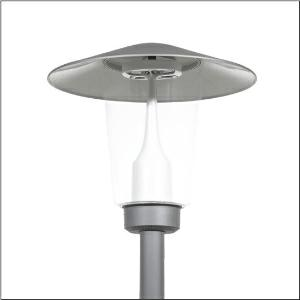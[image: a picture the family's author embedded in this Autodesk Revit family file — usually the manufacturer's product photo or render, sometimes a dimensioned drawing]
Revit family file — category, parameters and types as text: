
# Revit family: pilzleuchte_iq___p1_0a_5xa5235lf14hp_c758
name_source: partatom
category: Lighting Fixtures
units: mm (PartAtom-declared; Revit-internal decimal feet)

## family parameters
Cut with Voids When Loaded = No
Host = Face
Light Source = No
Part Type = Normal
Room Calculation Point = No
Round Connector Dimension = Use Diameter
Shared = No

## types (1)
- --- (1 x LED, 4960 lm, 33.6 W, 4000K)
    Apparent Load = 34 VA
    CIE Flux Codes = 35 64 90 96 100
    Color Rendering = 70
    Color Temperature = 4000K
    Default Elevation = 1800 mm
    Description = Mushroom Luminaire iQ, mast luminaire, Module 540 iQ-SR, primary light control with 3 zone facetted reflector, of plastic, silver coated, highly specular, structured, primary optical cover: cover, of PMMA, transparent, light distribution: P1.0a, light emission: direct distribution, primary light characteristic: strongly asymmetric, installation type: post-top, LED, High Power LED, rated luminous flux: 4.960lm, luminous efficacy: 148lm/W, light colour: 740, colour temperature: 4000K, control gear: ECG iQ, control: presetting dimming logarithmic, Street-Remote, Auto-Match, Temp-Guard, Lumen-Switch, Night-Set, Smart-Wire, Light-Fading, Desk-Remote (wireless, voltage-free reading and setting of iQ features in the workshop via application-optimized NFC function/RFID function), optimised constant luminous flux control (CLO 2.0), with terminal, 6-pole, max. 2.5mm², mains connection: 230..240V, AC, 50/60Hz, start of lifetime: 34W, end of service life: 36W, reduction: 15W, luminaire housing, upper part, of glass-fibre reinforced polyester, coated, Siteco® metallic grey (DB 702S), diameter: 650mm, height: 586mm, spigot size: d x l = 76 x 70mm (post-top) | with reducer (optional accessory) 60 x 70mm, post-top mast mounting element, of diecast aluminium, coated, Siteco® metallic grey (DB 702S), Module 540 iQ-SR, traffic white (RAL 9016), equipment: Power, protection rating (complete): IP65, insulation class (complete): insulation class II (safety insulation), certification: CE, ENEC, VDE, packaging unit: 1 piece

Light Distribution: P1.0a
    Height = 586 mm
    Lamp = 1 x LED
    Lamp Light Flux = 4960 lm
    Lamp Power = 33.6 W
    Lamp count = 1
    Length = 650 mm
    Luminous efficacy = 148 lm/W
    Manufacturer = Siteco
    ModVariant = No
    Model = 5XA5235LF14HP
    Number of Poles = 1
    OnlyDefault = Yes
    Power Factor = 1
    Product Name = Pilzleuchte iQ | P1.0a
    Product group = mast luminaire | pylon top
    ProductGroupID = 6100
    Protection Class = Protection class II
    Protection Degree = IP 65
    RLX_Detail_Level = 1
    RLX_Emergency_Light_Flux = 0 lm
    RLX_Emergency_Type = 0
    RLX_Emergency_Type_DB = No
    RlxData = <blob elided: 51953 chars, md5=2b1cf024>
    Socket = socket
    Standby Power = 0 W
    System Light Flux = 4960 lm
    System Power = 34 W
    Type Comments = factory setting: luminous flux: 100 % | dim-lin: 254 | 695 mA
    Type Image = l_1006077.jpg
    URL = http://relux.com
    VarID = @adj_144735
    Voltage = 0 V
    Weight = 0.00 kg
    Width = 0 mm  [stored 0 ft]

note: [stored X ft] marks values corroborated as IEEE doubles in the binary element streams (Revit-internal decimal feet)

## geometry (parser evidence)
native form markers: Blend x4, Sweep x14
no freeform markers — native parametric forms only
